# Revit family: ALBERO
name_source: partatom
category: Mass
revit_build: Autodesk Vasari (Build: 20130926_1200(x64))
units: mm (PartAtom-declared; Revit-internal decimal feet)

## types (3) — shared parameters
Ch 10 pianta = 4 m
Default Elevation = 1 m

## per-type parameters (varying)
| type | Ch 1 pianta | Ch 2 pianta | Ch 3 pianta | Ch 4 pianta | Ch 5 pianta | Ch 6 pianta | Ch 7 pianta | Ch 8 pianta | Ch 9 pianta | Chioma1 | Chioma10 | Chioma2 | Chioma3 | Chioma4 | Chioma5 | Chioma6 | Chioma7 | Chioma8 | Chioma9 | FT pianta | Fine chioma | Fino Tronco |
| 10 metri | 2 m | 4 m | 4 m | 5 m | 5 m | 6 m | 5 m | 5 m | 5 m | 4 m | 10 m | 5 m | 6 m | 7 m | 8 m | 8 m | 9 m | 9 m | 9 m | 1 m | 10 m | 3 m |
| 8 metri | 1 m | 4 m | 4 m | 4 m | 5 m | 5 m | 5 m | 5 m | 4 m | 3 m | 9 m | 5 m | 5 m | 6 m | 7 m | 8 m | 8 m | 8 m | 8 m | 1 m | 9 m | 2 m |
| 6 metri | 1 m | 3 m | 3 m | 4 m | 4 m | 5 m | 4 m | 4 m | 4 m | 2 m | 8 m | 4 m | 5 m | 5 m | 7 m | 7 m | 7 m | 8 m | 8 m | 0 m | 8 m | 2 m |

## geometry (parser evidence)
native form markers: Blend x12, Sweep x2
no freeform markers — native parametric forms only
